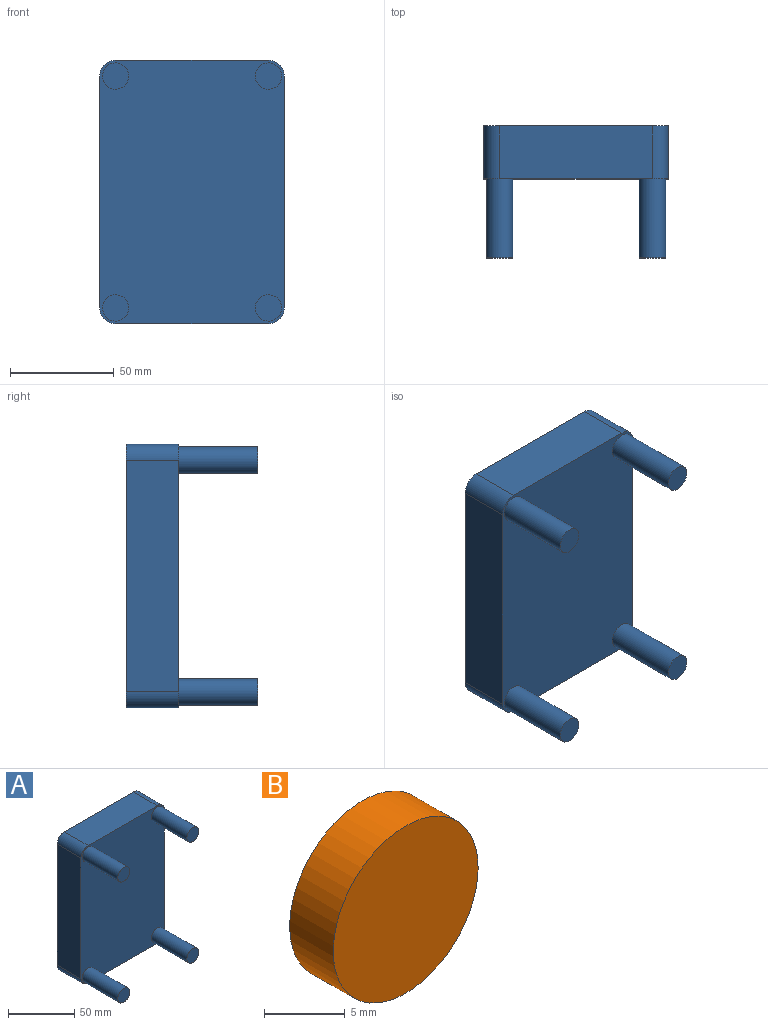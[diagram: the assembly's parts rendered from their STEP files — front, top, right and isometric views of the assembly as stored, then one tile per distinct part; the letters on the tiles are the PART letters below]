
ASSEMBLY  parts=2 mates=1
PART A: 27 faces, bbox 88.9x63.5x127 mm
  f0: plane 127x88.9mm, normal (0,1,0), area 2565.4mm2, adj f1,f2,f3,f4,f5,f6,f7,f8
  f1: plane 73.66x25.4mm, normal (0,0,-1), area 1871mm2, adj f0,f2,f8,f9
  f2: cylinder r=7.62mm len=25.4mm, axis (0,1,0), area 304mm2, adj f0,f1,f3,f9
  f3: plane 111.76x25.4mm, normal (1,0,0), area 2838.7mm2, adj f0,f2,f4,f9
  f4: cylinder r=7.62mm len=25.4mm, axis (0,1,0), area 304mm2, adj f0,f3,f5,f9
  f5: plane 73.66x25.4mm, normal (0,0,1), area 1871mm2, adj f0,f4,f6,f9
  f6: cylinder r=7.62mm len=25.4mm, axis (0,1,0), area 304mm2, adj f0,f5,f7,f9
  f7: plane 111.76x25.4mm, normal (-1,0,0), area 2838.7mm2, adj f0,f6,f8,f9
  f8: cylinder r=7.62mm len=25.4mm, axis (0,1,0), area 304mm2, adj f0,f1,f7,f9
  f9: plane 127x88.9mm, normal (0,-1,0), area 10733.7mm2, adj f1,f2,f3,f4,f5,f6,f7,f8
  f10: plane 63.5x12.7mm, normal (0,0,1), area 806.5mm2, adj f0,f11,f17,f18
  f11: cylinder r=6.35mm len=12.7mm, axis (0,1,0), area 126.7mm2, adj f0,f10,f12,f18
  f12: plane 101.6x12.7mm, normal (-1,0,0), area 1290.3mm2, adj f0,f11,f13,f18
  f13: cylinder r=6.35mm len=12.7mm, axis (0,1,0), area 126.7mm2, adj f0,f12,f14,f18
  f14: plane 63.5x12.7mm, normal (0,0,-1), area 806.5mm2, adj f0,f13,f15,f18
  f15: cylinder r=6.35mm len=12.7mm, axis (0,1,0), area 126.7mm2, adj f0,f14,f16,f18
  f16: plane 101.6x12.7mm, normal (1,0,0), area 1290.3mm2, adj f0,f15,f17,f18
  f17: cylinder r=6.35mm len=12.7mm, axis (0,1,0), area 126.7mm2, adj f0,f10,f16,f18
  f18: plane 114.3x76.2mm, normal (0,1,0), area 8675mm2, adj f10,f11,f12,f13,f14,f15,f16,f17
  f19: cylinder r=6.35mm len=38.1mm, axis (0,1,0), area 1520.1mm2, adj f9,f20
  f20: plane 12.7x12.7mm, normal (0,-1,0), area 126.7mm2, adj f19
  f21: cylinder r=6.35mm len=38.1mm, axis (0,1,0), area 1520.1mm2, adj f9,f22
  f22: plane 12.7x12.7mm, normal (0,-1,0), area 126.7mm2, adj f21
  f23: cylinder r=6.35mm len=38.1mm, axis (0,1,0), area 1520.1mm2, adj f9,f24
  f24: plane 12.7x12.7mm, normal (0,-1,0), area 126.7mm2, adj f23
  f25: cylinder r=6.35mm len=38.1mm, axis (0,1,0), area 1520.1mm2, adj f9,f26
  f26: plane 12.7x12.7mm, normal (0,-1,0), area 126.7mm2, adj f25
PART B: 3 faces, bbox 12.7x3.8x12.7 mm
  f0: cylinder r=6.35mm len=12.7mm, axis (0,1,0), area 152mm2, adj f1,f2
  f1: plane 12.7x12.7mm, normal (0,-1,0), area 126.7mm2, adj f0
  f2: plane 12.7x12.7mm, normal (0,1,0), area 126.7mm2, adj f0
PLACE A t=(-134.41,-22.71,-71.01)mm
PLACE B rot(axis=(0,1,0),0deg) t=(-103.93,-31.6,-20.21)mm
MATE planar B.f0 <-> A.f18  axis (0,-1,0) through (-103.93,-35.41,-20.21)mm
